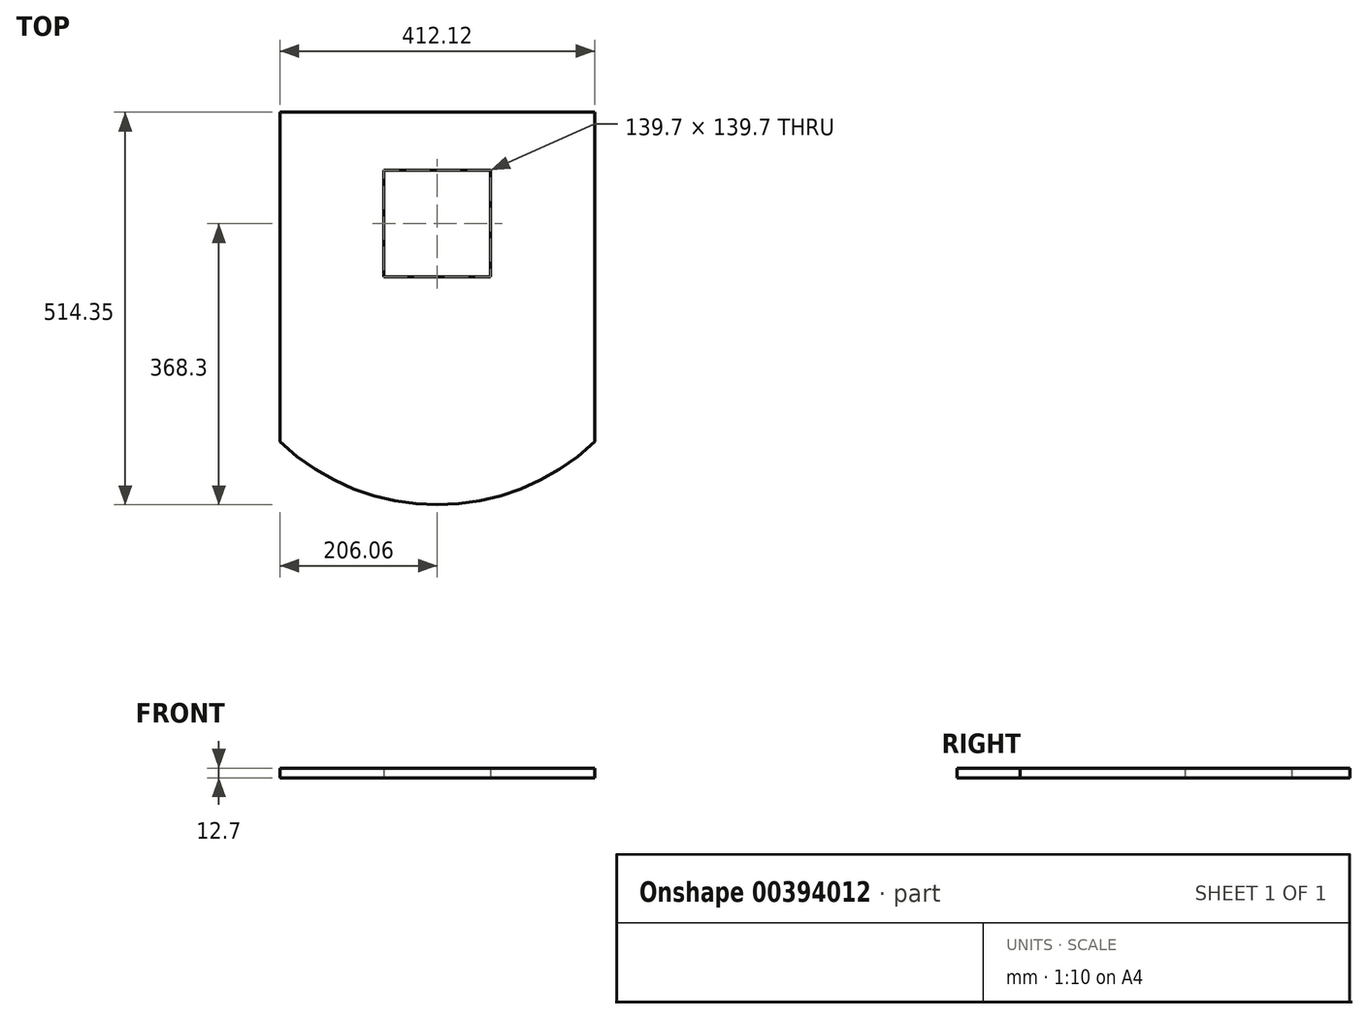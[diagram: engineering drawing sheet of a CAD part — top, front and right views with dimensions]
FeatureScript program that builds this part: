
annotation { "Feature Type Name" : "Feature", "Feature Type Description" : "" }
export const myFeature = defineFeature(function(context is Context, id is Id, definition is map)
    precondition{}
    {
        {
            var Q0;
            Q0=qCreatedBy(makeId("Top.planeOp"),FACE);
            var sketch = newSketch(context, id + "F0", { "sketchPlane" : qUnion([Q0])});
            skArc(sketch, "E0", {"start": v(-206.06, -215.9) * mm, "mid": v(0, -298.45) * mm, "end": v(206.06, -215.9) * mm});
            skLineSegment(sketch, "E1.bottom", {"start": v(-69.85, 139.7) * mm, "end": v(69.85, 139.7) * mm});
            skLineSegment(sketch, "E1.top", {"start": v(-69.85, 0) * mm, "end": v(69.85, 0) * mm});
            skLineSegment(sketch, "E1.left", {"start": v(-69.85, 139.7) * mm, "end": v(-69.85, 0) * mm});
            skLineSegment(sketch, "E1.right", {"start": v(69.85, 139.7) * mm, "end": v(69.85, 0) * mm});
            skLineSegment(sketch, "E2", {"start": v(-69.85, 139.7) * mm, "end": v(-69.85, 215.9) * mm, "construction": true});
            skLineSegment(sketch, "E3", {"start": v(-206.06, 215.9) * mm, "end": v(206.06, 215.9) * mm});
            skLineSegment(sketch, "E4", {"start": v(206.06, 215.9) * mm, "end": v(206.06, -215.9) * mm});
            skLineSegment(sketch, "E5", {"start": v(-206.06, 215.9) * mm, "end": v(-206.06, -215.9) * mm});
            skSolve(sketch);
        }
        {
            var Q0;
            Q0=makeQuery(id+"F0.imprint","IMPRINT",FACE,{"disambiguationData":[TD([[makeQuery(id+"F0.imprint","IMPRINT",EDGE,{"derivedFrom":sQuery(id+"F0.wireOp",EDGE,"E0")}),1.0]])]});
            extrude(context, id + "F1", {"entities" : qUnion([Q0]), "depth" : 12.7 * mm});
        }
        {
            var Q0;
            Q0=qSketchRegion(id+"F0",true);
            extrude(context, id + "F2", {"entities" : qUnion([Q0]), "operationType" : NewBodyOperationType.ADD, "depth" : 12.7 * mm});
        }
    });
